FCSTD DOCUMENT  (FreeCAD 0.18R16110 (Git))
Label: 8sideP
License: All rights reserved
LicenseURL: http://en.wikipedia.org/wiki/All_rights_reserved
objects: Sketcher::SketchObject×1
note: 1 computed .brp shape members not serialized (recipe doc carries the construction recipe); baked Part::Feature solids carry a one-line shape summary decoded from their .brp

FEATURE [Sketcher::SketchObject] Sketch
  sketch-geometry (41):
    g0: LineSegment [constr] StartX=-603.706 StartY=-234.1 StartZ=0 EndX=-261.351 EndY=-592.419 EndZ=0
    g1: LineSegment [constr] StartX=-261.351 StartY=-592.419 StartZ=0 EndX=234.1 EndY=-603.706 EndZ=0
    g2: LineSegment [constr] StartX=234.1 StartY=-603.706 StartZ=0 EndX=592.419 EndY=-261.351 EndZ=0
    g3: LineSegment [constr] StartX=592.419 StartY=-261.351 StartZ=0 EndX=603.706 EndY=234.1 EndZ=0
    g4: LineSegment [constr] StartX=603.706 StartY=234.1 StartZ=0 EndX=261.351 EndY=592.419 EndZ=0
    g5: LineSegment [constr] StartX=261.351 StartY=592.419 StartZ=0 EndX=-234.1 EndY=603.706 EndZ=0
    g6: LineSegment [constr] StartX=-234.1 StartY=603.706 StartZ=0 EndX=-592.419 EndY=261.351 EndZ=0
    g7: LineSegment [constr] StartX=-592.419 StartY=261.351 StartZ=0 EndX=-603.706 EndY=-234.1 EndZ=0
    g8: Circle [constr] CenterX=0 CenterY=0 CenterZ=0 NormalX=0 NormalY=0 NormalZ=1 AngleXU=0 Radius=647.506
    g9: LineSegment [constr] StartX=-249.993 StartY=-103.551 StartZ=0 EndX=-103.551 EndY=-249.993 EndZ=0
    g10: LineSegment [constr] StartX=-103.551 StartY=-249.993 StartZ=0 EndX=103.551 EndY=-249.993 EndZ=0
    g11: LineSegment [constr] StartX=103.551 StartY=-249.993 StartZ=0 EndX=249.993 EndY=-103.551 EndZ=0
    g12: LineSegment [constr] StartX=249.993 StartY=-103.551 StartZ=0 EndX=249.993 EndY=103.551 EndZ=0
    g13: LineSegment [constr] StartX=249.993 StartY=103.551 StartZ=0 EndX=103.551 EndY=249.993 EndZ=0
    g14: LineSegment [constr] StartX=103.551 StartY=249.993 StartZ=0 EndX=-103.551 EndY=249.993 EndZ=0
    g15: LineSegment [constr] StartX=-103.551 StartY=249.993 StartZ=0 EndX=-249.993 EndY=103.551 EndZ=0
    g16: LineSegment [constr] StartX=-249.993 StartY=103.551 StartZ=0 EndX=-249.993 EndY=-103.551 EndZ=0
    g17: Circle [constr] CenterX=0 CenterY=0 CenterZ=0 NormalX=0 NormalY=0 NormalZ=1 AngleXU=0 Radius=270.591
    g18: LineSegment [constr] StartX=-592.419 StartY=261.351 StartZ=0 EndX=-103.551 EndY=249.993 EndZ=0
    g19: LineSegment [constr] StartX=-234.1 StartY=603.706 StartZ=0 EndX=103.551 EndY=249.993 EndZ=0
    g20: LineSegment [constr] StartX=261.351 StartY=592.419 StartZ=0 EndX=249.993 EndY=103.551 EndZ=0
    g21: LineSegment [constr] StartX=603.706 StartY=234.1 StartZ=0 EndX=249.993 EndY=-103.551 EndZ=0
    g22: LineSegment [constr] StartX=592.419 StartY=-261.351 StartZ=0 EndX=103.551 EndY=-249.993 EndZ=0
    g23: LineSegment [constr] StartX=234.1 StartY=-603.706 StartZ=0 EndX=-103.553 EndY=-250 EndZ=0
    g24: LineSegment [constr] StartX=-261.351 StartY=-592.419 StartZ=0 EndX=-249.993 EndY=-103.551 EndZ=0
    g25: LineSegment [constr] StartX=-603.706 StartY=-234.1 StartZ=0 EndX=-250 EndY=103.553 EndZ=0
    g26: LineSegment StartX=-406 StartY=406 StartZ=0 EndX=-406 EndY=-406 EndZ=0
    g27: LineSegment StartX=-406 StartY=-406 StartZ=0 EndX=406 EndY=-406 EndZ=0
    g28: LineSegment StartX=406 StartY=-406 StartZ=0 EndX=406 EndY=406 EndZ=0
    g29: LineSegment StartX=406 StartY=406 StartZ=0 EndX=-406 EndY=406 EndZ=0
    g30: LineSegment StartX=0 StartY=0 StartZ=0 EndX=-248.375 EndY=83.3896 EndZ=0
    g31: LineSegment StartX=0 StartY=0 StartZ=0 EndX=-89.7855 EndY=246.135 EndZ=0
    g32: LineSegment StartX=0 StartY=0 StartZ=0 EndX=136.344 EndY=223.728 EndZ=0
    g33: LineSegment StartX=0 StartY=0 StartZ=0 EndX=-26.2902 EndY=-260.678 EndZ=0
    g34: LineSegment StartX=0 StartY=0 StartZ=0 EndX=-220.127 EndY=-142.085 EndZ=0
    g35: LineSegment StartX=136.344 StartY=223.728 StartZ=0 EndX=150.495 EndY=165.42 EndZ=0
    g36: LineSegment StartX=92.1871 StartY=151.27 StartZ=0 EndX=150.495 EndY=165.42 EndZ=0
    g37: LineSegment StartX=0 StartY=0 StartZ=0 EndX=259.91 EndY=33.0233 EndZ=0
    g38: LineSegment StartX=259.91 StartY=33.0233 StartZ=0 EndX=223.17 EndY=-14.4123 EndZ=0
    g39: LineSegment StartX=223.17 StartY=-14.4123 StartZ=0 EndX=175.734 EndY=22.3282 EndZ=0
    g40: Circle CenterX=0 CenterY=0 CenterZ=0 NormalX=0 NormalY=0 NormalZ=1 AngleXU=0 Radius=80
  constraints (92):
    c: Coincident(g0,g1)
    c: Coincident(g1,g2)
    c: Coincident(g2,g3)
    c: Coincident(g3,g4)
    c: Coincident(g4,g5)
    c: Coincident(g5,g6)
    c: Equal(g0, g1-g7) x7
    c: PointOnObject(g0,g8)
    c: PointOnObject(g1,g8)
    c: PointOnObject(g2,g8)
    c: PointOnObject(g3,g8)
    c: PointOnObject(g4,g8)
    c: PointOnObject(g5,g8)
    c: PointOnObject(g6,g8)
    c: Coincident(g8,g-1)
    c: Coincident(g9,g10)
    c: Coincident(g10,g11)
    c: Coincident(g11,g12)
    c: Coincident(g12,g13)
    c: Coincident(g13,g14)
    c: Coincident(g14,g15)
    c: Coincident(g15,g16)
    c: Coincident(g16,g9)
    c: Equal(g9, g10-g16) x7
    c: PointOnObject(g9,g17)
    c: PointOnObject(g10,g17)
    c: PointOnObject(g11,g17)
    c: PointOnObject(g12,g17)
    c: PointOnObject(g13,g17)
    c: PointOnObject(g14,g17)
    c: PointOnObject(g15,g17)
    c: PointOnObject(g16,g17)
    c: Coincident(g17,g-1)
    c: Horizontal(g10)
    c: Coincident(g18,g6)
    c: Coincident(g18,g14)
    c: Coincident(g19,g5)
    c: Coincident(g19,g13)
    c: Coincident(g20,g4)
    c: Coincident(g20,g12)
    c: Coincident(g21,g3)
    c: Coincident(g21,g11)
    c: Coincident(g22,g2)
    c: Coincident(g22,g10)
    c: Coincident(g23,g1)
    c: Coincident(g24,g0)
    c: Coincident(g24,g9)
    c: Coincident(g25,g0)
    c: Coincident(g0,g7)
    c: Coincident(g6,g7)
    c: PointOnObject(g0,g8)
    c: Distance(g24) = 489
    c: Coincident(g26,g27)
    c: Coincident(g27,g28)
    c: Coincident(g28,g29)
    c: Coincident(g29,g26)
    c: Equal(g26,g27)
    c: Equal(g26,g28)
    c: Equal(g26,g29)
    c: Horizontal(g27)
    c: DistanceX(g27,g27) = 812
    c: Coincident(g30,g-1)
    c: Coincident(g31,g30)
    c: Coincident(g32,g30)
    c: Coincident(g33,g30)
    c: Coincident(g34,g30)
    c: Angle(g34,g33) = 0.897099
    c: Angle(g30,g34) = 0.897099
    c: Angle(g31,g30) = 0.897099
    c: Angle(g32,g31) = 0.897099
    c: Equal(g33,g34)
    c: Equal(g34,g30)
    c: Equal(g30,g31)
    c: Equal(g31,g32)
    c: Distance(g31) = 262
    c: Coincident(g35,g32)
    c: PointOnObject(g36,g32)
    c: Coincident(g36,g35)
    c: Angle(g35,g36) = 1.5708
    c: Angle(g32,g35) = 0.785398
    c: Distance(g35) = 60
    c: Coincident(g37,g30)
    c: Equal(g37,g32)
    c: Coincident(g37,g38)
    c: Coincident(g38,g39)
    c: PointOnObject(g39,g37)
    c: Angle(g38,g39) = 1.5708
    c: Angle(g37,g38) = 0.785398
    c: Distance(g38) = 60
    c: Angle(g37,g32) = 0.897099
    c: Coincident(g40,g30)
    c: Radius(g40) = 80
